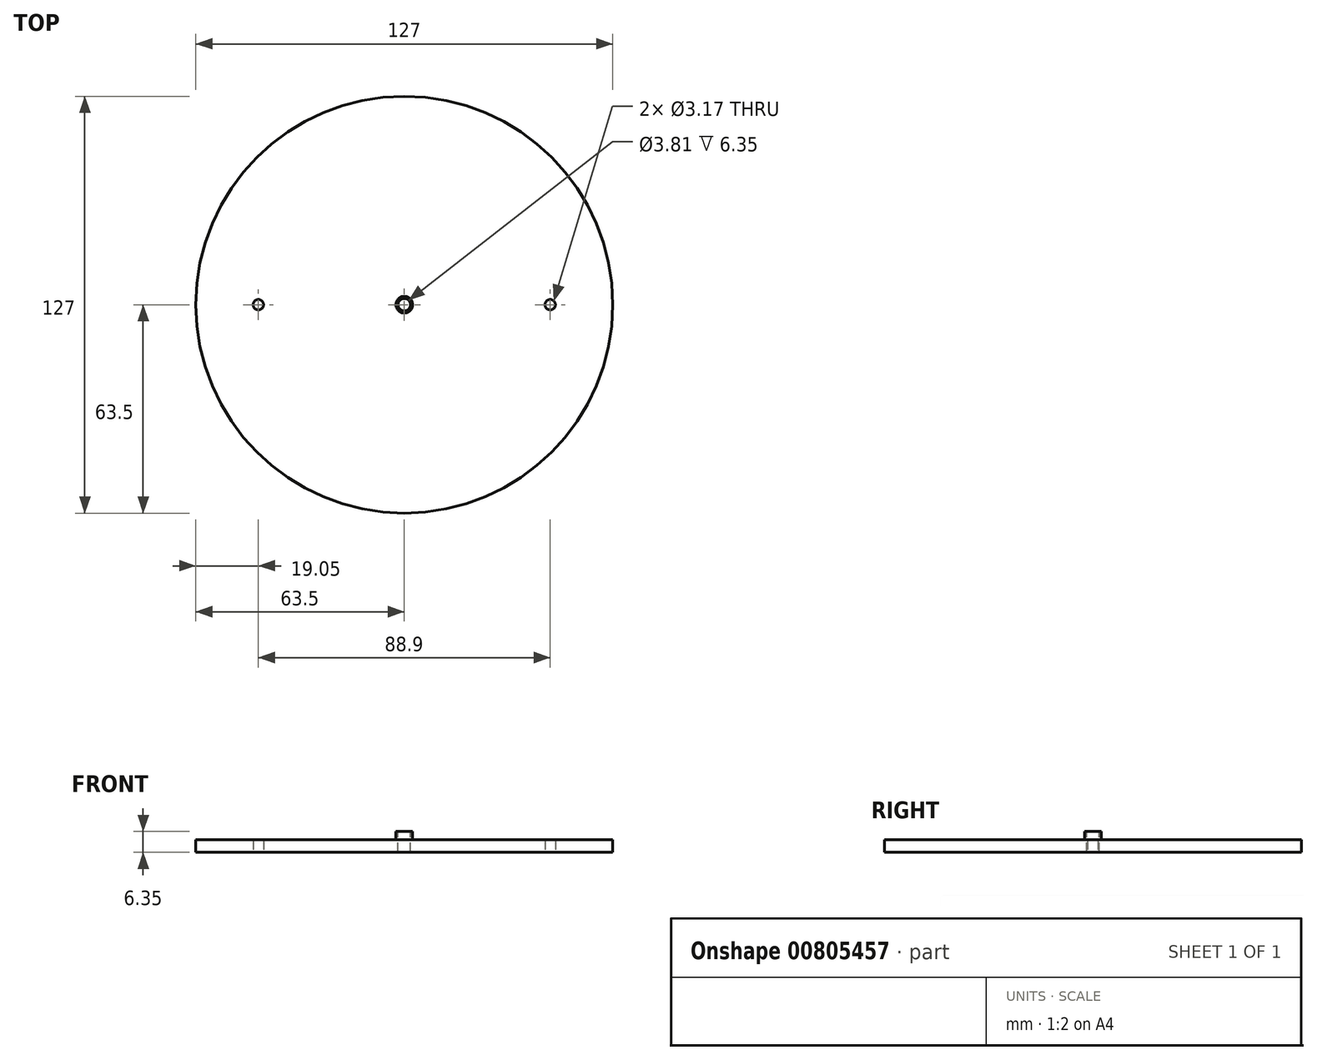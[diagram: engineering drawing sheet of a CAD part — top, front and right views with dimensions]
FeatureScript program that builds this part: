
annotation { "Feature Type Name" : "Feature", "Feature Type Description" : "" }
export const myFeature = defineFeature(function(context is Context, id is Id, definition is map)
    precondition{}
    {
        {
            var Q0;
            Q0=qCreatedBy(makeId("Top.planeOp"),FACE);
            var sketch = newSketch(context, id + "F0", { "sketchPlane" : qUnion([Q0])});
            skCircle(sketch, "E0", {"center": v(0, 0) * mm, "radius": 63.5 * mm});
            skCircle(sketch, "E1", {"center": v(0, 0) * mm, "radius": 2.54 * mm});
            skSolve(sketch);
        }
        {
            var Q0;
            Q0=makeQuery(id+"F0.imprint","IMPRINT",FACE,{"disambiguationData":[TD([[makeQuery(id+"F0.imprint","IMPRINT",EDGE,{"derivedFrom":sQuery(id+"F0.wireOp",EDGE,"E1")}),1.0]])]});
            extrude(context, id + "F1", {"entities" : qUnion([Q0]), "depth" : 6.35 * mm, "offsetDistance" : 25.4 * mm});
        }
        {
            var Q0;
            Q0 = qSketchRegion(id + "F0", true);
            extrude(context, id + "F2", {"entities" : qUnion([Q0]), "operationType" : NewBodyOperationType.ADD, "depth" : 3.8 * mm, "offsetDistance" : 25.4 * mm});
        }
        {
            var Q0;
            Q0=makeQuery(id+"F1.opExtrude","CAP_FACE",FACE,{"disambiguationData":[OSD([sQuery(id+"F0.wireOp",EDGE,"E1")])],"isStart":false});
            var sketch = newSketch(context, id + "F3", { "sketchPlane" : qUnion([Q0])});
            skCircle(sketch, "E2", {"center": v(0, 0) * mm, "radius": 1.9 * mm});
            skSolve(sketch);
        }
        {
            var Q0;
            Q0=makeQuery(id+"F3.imprint","IMPRINT",FACE,{"disambiguationData":[TD([[makeQuery(id+"F3.imprint","IMPRINT",EDGE,{"derivedFrom":sQuery(id+"F3.wireOp",EDGE,"E2")}),1.0]])]});
            extrude(context, id + "F4", {"entities" : qUnion([Q0]), "operationType" : NewBodyOperationType.REMOVE, "oppositeDirection" : true, "depth" : 40.64 * mm, "offsetDistance" : 25.4 * mm});
        }
        {
            var Q0;
            {var subQ0=sQuery(id+"F0.wireOp",EDGE,"E1");Q0=makeQuery(id+"F2.boolean.opBoolean","MERGE",FACE,{"derivedFrom":[makeQuery(id+"F1.opExtrude","CAP_FACE",FACE,{"disambiguationData":[OSD([subQ0])],"isStart":true}),makeQuery(id+"F2.opExtrude","CAP_FACE",FACE,{"disambiguationData":[OSD([sQuery(id+"F0.wireOp",EDGE,"E0"),subQ0])],"isStart":true})]});}
            var sketch = newSketch(context, id + "F5", { "sketchPlane" : qUnion([Q0])});
            skCircle(sketch, "E3", {"center": v(44.45, 0) * mm, "radius": 1.59 * mm});
            skCircle(sketch, "E4", {"center": v(-44.45, 0) * mm, "radius": 1.59 * mm});
            skLineSegment(sketch, "E5", {"start": v(44.45, 0) * mm, "end": v(0, 0) * mm, "construction": true});
            skLineSegment(sketch, "E6", {"start": v(0, 0) * mm, "end": v(-44.45, 0) * mm, "construction": true});
            skSolve(sketch);
        }
        {
            var Q0;
            Q0=makeQuery(id+"F5.imprint","IMPRINT",FACE,{"disambiguationData":[TD([[makeQuery(id+"F5.imprint","IMPRINT",EDGE,{"derivedFrom":sQuery(id+"F5.wireOp",EDGE,"E3")}),1.0]])]});
            var Q1;
            Q1=makeQuery(id+"F5.imprint","IMPRINT",FACE,{"disambiguationData":[TD([[makeQuery(id+"F5.imprint","IMPRINT",EDGE,{"derivedFrom":sQuery(id+"F5.wireOp",EDGE,"E4")}),1.0]])]});
            extrude(context, id + "F6", {"entities" : qUnion([Q0, Q1]), "operationType" : NewBodyOperationType.REMOVE, "oppositeDirection" : true, "depth" : 25.4 * mm, "offsetDistance" : 25.4 * mm});
        }
    });
